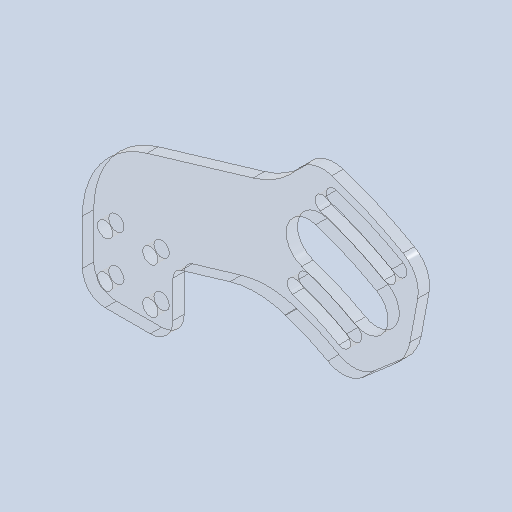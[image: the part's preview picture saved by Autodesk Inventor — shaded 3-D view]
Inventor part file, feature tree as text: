
AUTODESK INVENTOR PART (.ipt)
format: ipt  version: 2023 (Build 270158000, 158)  size: 166,400 bytes
history: native  units: in
note: dims shown in document units (in); Inventor stores cm internally (conversion verified against a paired STEP export)
features: other x3, sketch x1
ambient origin geometry x8: Origin, YZ Plane, XZ Plane, XY Plane, X Axis, Y Axis, Z Axis, Center Point
bodies: Solid1 (feature_tree)
feature tree (4):
  other  "IntakeForearm.ipt"
  other  "Solid1::IntakeForearm.ipt"
  other  "TaggingFeature1"
  sketch  "Sketch1"  dims[d0=0.3937in]
